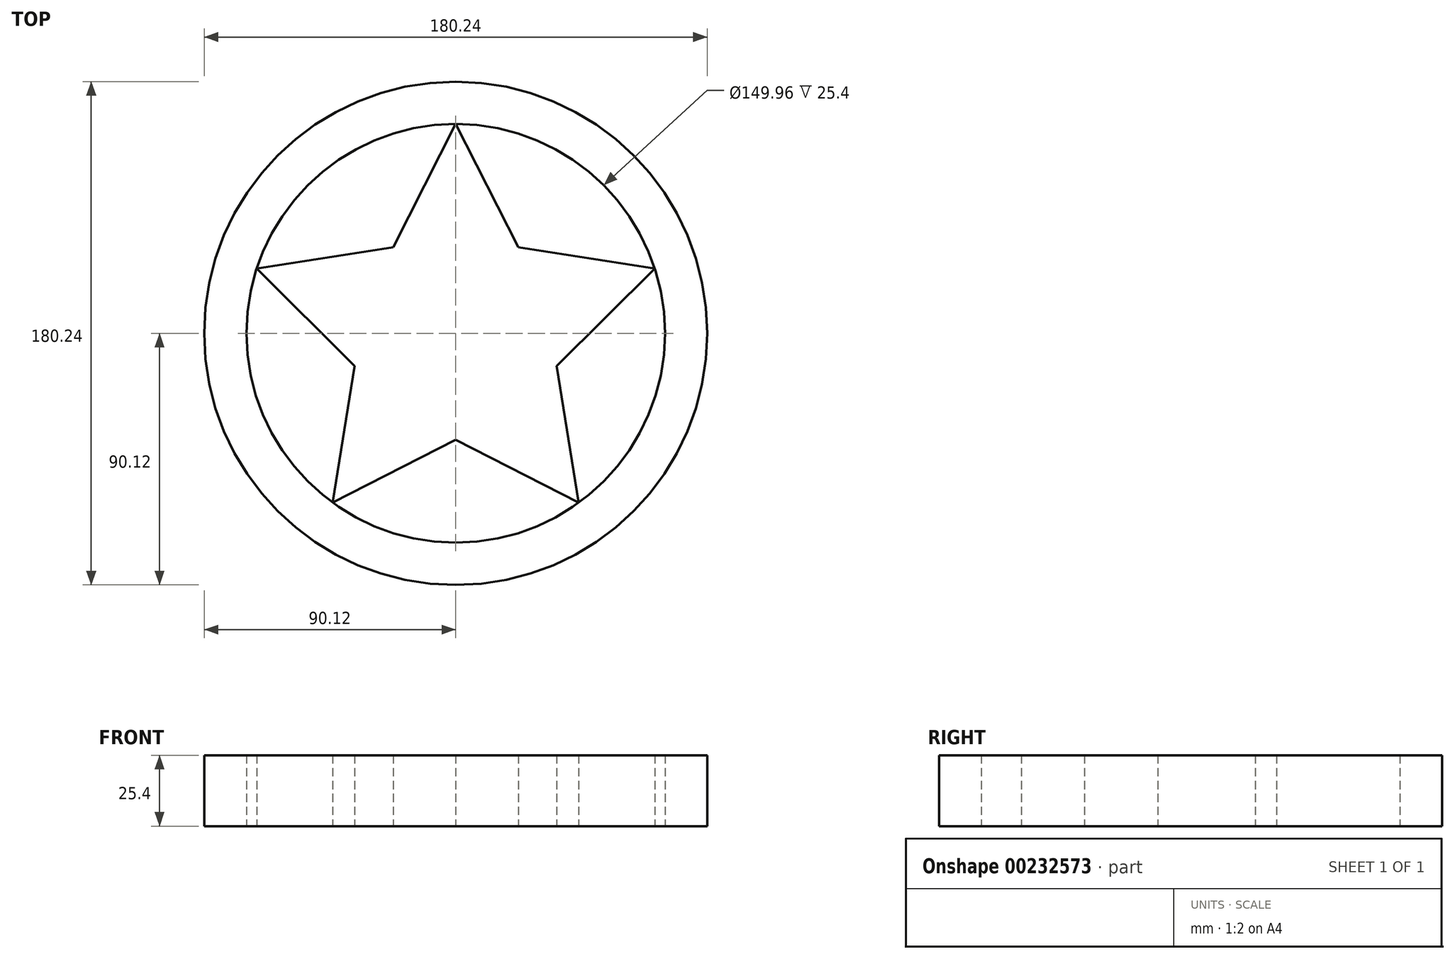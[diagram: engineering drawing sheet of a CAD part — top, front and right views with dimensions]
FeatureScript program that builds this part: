
annotation { "Feature Type Name" : "Feature", "Feature Type Description" : "" }
export const myFeature = defineFeature(function(context is Context, id is Id, definition is map)
    precondition{}
    {
        {
            var Q0;
            Q0=qCreatedBy(makeId("Top.planeOp"),FACE);
            var sketch = newSketch(context, id + "F0", { "sketchPlane" : qUnion([Q0])});
            skCircle(sketch, "E0", {"center": v(0, 0) * mm, "radius": 74.98 * mm});
            skLineSegment(sketch, "E1", {"start": v(0, 0) * mm, "end": v(0, 74.98) * mm});
            skLineSegment(sketch, "E2", {"start": v(-71.31, 23.17) * mm, "end": v(0, 0) * mm});
            skLineSegment(sketch, "E3", {"start": v(0, 0) * mm, "end": v(71.31, 23.17) * mm});
            skLineSegment(sketch, "E4", {"start": v(0, 0) * mm, "end": v(44.07, -60.66) * mm});
            skLineSegment(sketch, "E5", {"start": v(0, 0) * mm, "end": v(-44.07, -60.66) * mm});
            skLineSegment(sketch, "E6", {"start": v(0, 0) * mm, "end": v(-22.4, 30.82) * mm});
            skLineSegment(sketch, "E7", {"start": v(-22.4, 30.82) * mm, "end": v(-71.31, 23.17) * mm});
            skLineSegment(sketch, "E8", {"start": v(-22.4, 30.82) * mm, "end": v(0, 74.98) * mm});
            skLineSegment(sketch, "E9.MirrorCS", {"start": v(22.4, 30.82) * mm, "end": v(71.31, 23.17) * mm});
            skLineSegment(sketch, "E10.MirrorCS", {"start": v(22.4, 30.82) * mm, "end": v(0, 74.98) * mm});
            skLineSegment(sketch, "E11.MirrorCS", {"start": v(0, 0) * mm, "end": v(22.4, 30.82) * mm});
            skLineSegment(sketch, "E12", {"start": v(0, 0) * mm, "end": v(-36.24, -11.77) * mm});
            skLineSegment(sketch, "E13", {"start": v(-71.31, 23.17) * mm, "end": v(-36.24, -11.77) * mm});
            skLineSegment(sketch, "E14", {"start": v(-36.24, -11.77) * mm, "end": v(-44.07, -60.66) * mm});
            skLineSegment(sketch, "E15", {"start": v(0, 0) * mm, "end": v(0, -38.1) * mm});
            skLineSegment(sketch, "E16", {"start": v(0, -38.1) * mm, "end": v(-44.07, -60.66) * mm});
            skLineSegment(sketch, "E17.MirrorCS", {"start": v(71.31, 23.17) * mm, "end": v(36.24, -11.77) * mm});
            skLineSegment(sketch, "E18.MirrorCS", {"start": v(36.24, -11.77) * mm, "end": v(44.07, -60.66) * mm});
            skLineSegment(sketch, "E19.MirrorCS", {"start": v(0, -38.1) * mm, "end": v(44.07, -60.66) * mm});
            skLineSegment(sketch, "E20.MirrorCS", {"start": v(0, 0) * mm, "end": v(36.24, -11.77) * mm});
            skCircle(sketch, "E21", {"center": v(0, 0) * mm, "radius": 90.12 * mm});
            skSolve(sketch);
        }
        {
            var Q0;
            Q0=makeQuery(id+"F0.imprint","IMPRINT",FACE,{"disambiguationData":[TD([[makeQuery(id+"F0.imprint","IMPRINT",EDGE,{"derivedFrom":sQuery(id+"F0.wireOp",EDGE,"E21")}),1.0]])]});
            var Q1;
            Q1=makeQuery(id+"F0.imprint","IMPRINT",FACE,{"disambiguationData":[TD([[makeQuery(id+"F0.imprint","IMPRINT",EDGE,{"derivedFrom":sQuery(id+"F0.wireOp",EDGE,"E2")}),-1.0]])]});
            var Q2;
            Q2=makeQuery(id+"F0.imprint","IMPRINT",FACE,{"disambiguationData":[TD([[makeQuery(id+"F0.imprint","IMPRINT",EDGE,{"derivedFrom":sQuery(id+"F0.wireOp",EDGE,"E1")}),1.0]])]});
            var Q3;
            Q3=makeQuery(id+"F0.imprint","IMPRINT",FACE,{"disambiguationData":[TD([[makeQuery(id+"F0.imprint","IMPRINT",EDGE,{"derivedFrom":sQuery(id+"F0.wireOp",EDGE,"E1")}),-1.0]])]});
            var Q4;
            Q4=makeQuery(id+"F0.imprint","IMPRINT",FACE,{"disambiguationData":[TD([[makeQuery(id+"F0.imprint","IMPRINT",EDGE,{"derivedFrom":sQuery(id+"F0.wireOp",EDGE,"E3")}),1.0]])]});
            var Q5;
            Q5=makeQuery(id+"F0.imprint","IMPRINT",FACE,{"disambiguationData":[TD([[makeQuery(id+"F0.imprint","IMPRINT",EDGE,{"derivedFrom":sQuery(id+"F0.wireOp",EDGE,"E3")}),-1.0]])]});
            var Q6;
            Q6=makeQuery(id+"F0.imprint","IMPRINT",FACE,{"disambiguationData":[TD([[makeQuery(id+"F0.imprint","IMPRINT",EDGE,{"derivedFrom":sQuery(id+"F0.wireOp",EDGE,"E4")}),1.0]])]});
            var Q7;
            Q7=makeQuery(id+"F0.imprint","IMPRINT",FACE,{"disambiguationData":[TD([[makeQuery(id+"F0.imprint","IMPRINT",EDGE,{"derivedFrom":sQuery(id+"F0.wireOp",EDGE,"E4")}),-1.0]])]});
            var Q8;
            Q8=makeQuery(id+"F0.imprint","IMPRINT",FACE,{"disambiguationData":[TD([[makeQuery(id+"F0.imprint","IMPRINT",EDGE,{"derivedFrom":sQuery(id+"F0.wireOp",EDGE,"E5")}),1.0]])]});
            var Q9;
            Q9=makeQuery(id+"F0.imprint","IMPRINT",FACE,{"disambiguationData":[TD([[makeQuery(id+"F0.imprint","IMPRINT",EDGE,{"derivedFrom":sQuery(id+"F0.wireOp",EDGE,"E5")}),-1.0]])]});
            var Q10;
            Q10=makeQuery(id+"F0.imprint","IMPRINT",FACE,{"disambiguationData":[TD([[makeQuery(id+"F0.imprint","IMPRINT",EDGE,{"derivedFrom":sQuery(id+"F0.wireOp",EDGE,"E2")}),1.0]])]});
            extrude(context, id + "F1", {"entities" : qUnion([Q0, Q1, Q2, Q3, Q4, Q5, Q6, Q7, Q8, Q9, Q10]), "depth" : 25.4 * mm});
        }
    });
